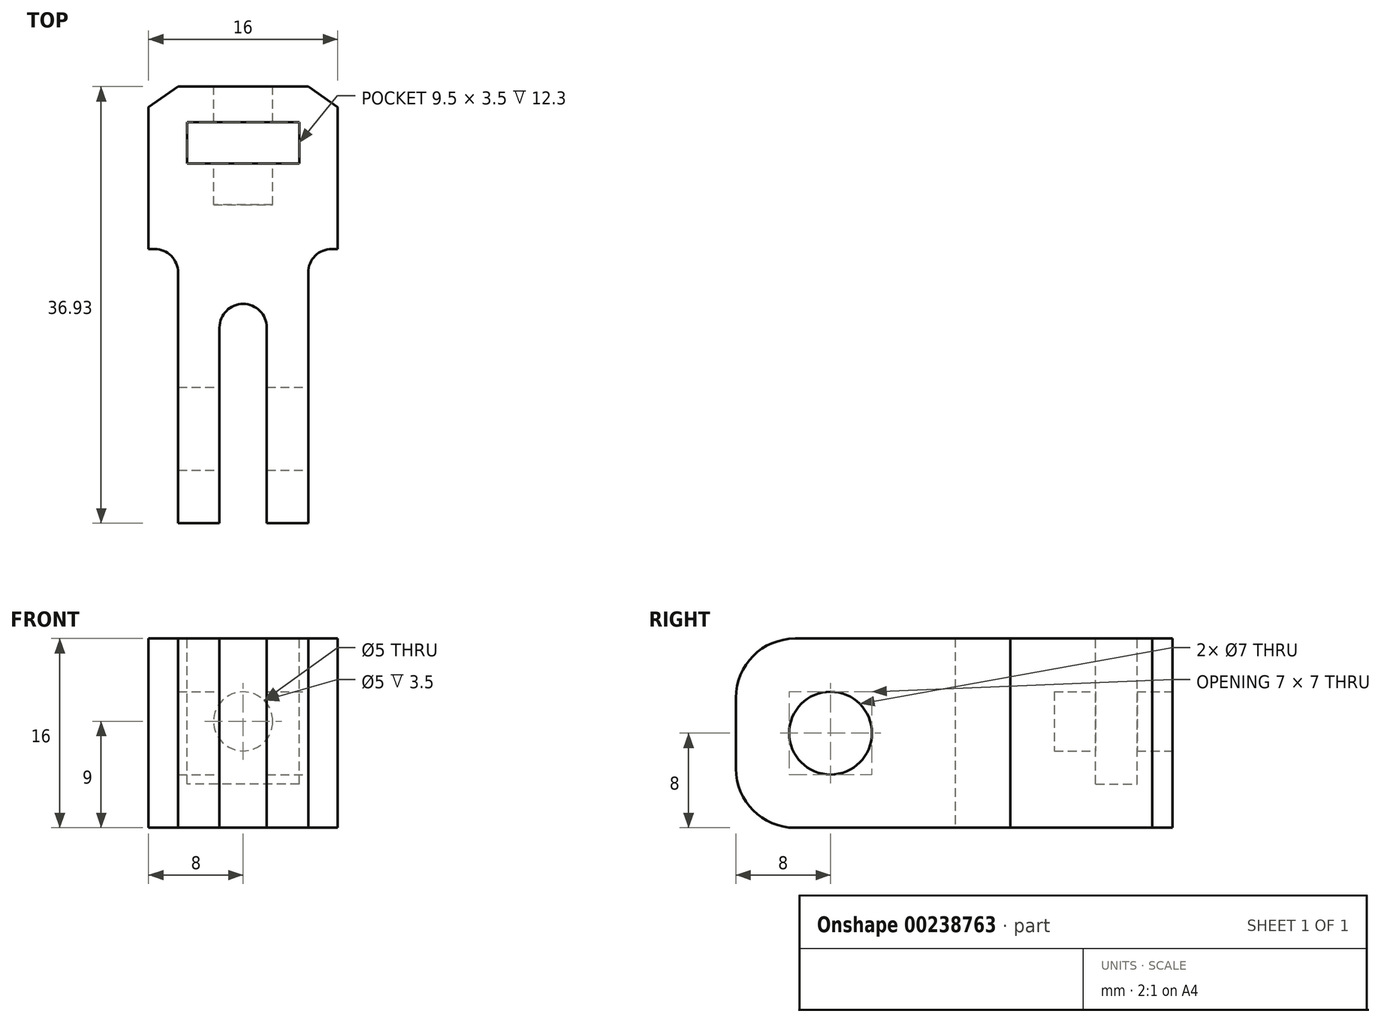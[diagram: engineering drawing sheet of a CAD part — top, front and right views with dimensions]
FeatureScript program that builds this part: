
annotation { "Feature Type Name" : "Feature", "Feature Type Description" : "" }
export const myFeature = defineFeature(function(context is Context, id is Id, definition is map)
    precondition{}
    {
        {
            var Q0;
            Q0=qCreatedBy(makeId("Top.planeOp"),FACE);
            var sketch = newSketch(context, id + "F0", { "sketchPlane" : qUnion([Q0])});
            skLineSegment(sketch, "E0.top", {"start": v(-5.5, -26) * mm, "end": v(-2, -26) * mm});
            skLineSegment(sketch, "E0.left", {"start": v(-5.5, -2.8) * mm, "end": v(-5.5, -26) * mm});
            skLineSegment(sketch, "E0.right", {"start": v(5.5, -2.8) * mm, "end": v(5.5, -26) * mm});
            skLineSegment(sketch, "E1.top", {"start": v(-2, -7.45) * mm, "end": v(2, -7.45) * mm});
            skLineSegment(sketch, "E1.left", {"start": v(-2, -26) * mm, "end": v(-2, -7.45) * mm});
            skLineSegment(sketch, "E1.right", {"start": v(2, -26) * mm, "end": v(2, -7.45) * mm});
            skLineSegment(sketch, "E2.trimOffspring", {"start": v(2, -26) * mm, "end": v(5.5, -26) * mm});
            skLineSegment(sketch, "E3.top", {"start": v(-5.5, 10.93) * mm, "end": v(5.5, 10.93) * mm});
            skLineSegment(sketch, "E4", {"start": v(0, 24.77) * mm, "end": v(0, -50.26) * mm, "construction": true});
            skPoint(sketch, "E4.startSnap0", {"position": v(0, 10.93) * mm});
            skPoint(sketch, "E4.endSnap0", {"position": v(0, -7.45) * mm});
            skLineSegment(sketch, "E5.top", {"start": v(-8, -2.8) * mm, "end": v(-5.5, -2.8) * mm});
            skLineSegment(sketch, "E5.left", {"start": v(-8, 9.2) * mm, "end": v(-8, -2.8) * mm});
            skLineSegment(sketch, "E5.right", {"start": v(8, 9.2) * mm, "end": v(8, -2.8) * mm});
            skPoint(sketch, "E5.middle", {"position": v(0, 3.2) * mm});
            skPoint(sketch, "E6.orphan", {"position": v(-5.5, 0) * mm});
            skLineSegment(sketch, "E7.trimOffspring", {"start": v(5.5, -2.8) * mm, "end": v(8, -2.8) * mm});
            skLineSegment(sketch, "E8", {"start": v(8, 9.2) * mm, "end": v(5.5, 10.93) * mm});
            skLineSegment(sketch, "E9", {"start": v(-5.5, 10.93) * mm, "end": v(-8, 9.2) * mm});
            skSolve(sketch);
        }
        {
            var Q0;
            Q0=qSketchRegion(id+"F0",true);
            extrude(context, id + "F1", {"entities" : qUnion([Q0]), "depth" : 16 * mm});
        }
        {
            var Q0;
            Q0=makeQuery(id+"F1.opExtrude","SWEPT_FACE",FACE,{"disambiguationData":[OSD([sQuery(id+"F0.wireOp",EDGE,"E3.top")])]});
            var sketch = newSketch(context, id + "F2", { "sketchPlane" : qUnion([Q0])});
            skCircle(sketch, "E10", {"center": v(0, 9) * mm, "radius": 2.5 * mm});
            skSolve(sketch);
        }
        {
            var Q0;
            Q0=qSketchRegion(id+"F2",true);
            extrude(context, id + "F3", {"entities" : qUnion([Q0]), "operationType" : NewBodyOperationType.REMOVE, "oppositeDirection" : true, "depth" : 10 * mm});
        }
        {
            var Q0;
            Q0=makeQuery(id+"F1.opExtrude","SWEPT_FACE",FACE,{"disambiguationData":[OSD([sQuery(id+"F0.wireOp",EDGE,"E0.right"),sQuery(id+"F0.wireOp",EDGE,"E3.right")])]});
            var sketch = newSketch(context, id + "F4", { "sketchPlane" : qUnion([Q0])});
            skCircle(sketch, "E11", {"center": v(-18, 8) * mm, "radius": 3.5 * mm});
            skSolve(sketch);
        }
        {
            var Q0;
            Q0=qSketchRegion(id+"F4",true);
            var Q1;
            Q1=makeQuery(id+"F1.opExtrude","SWEPT_FACE",FACE,{"disambiguationData":[OSD([sQuery(id+"F0.wireOp",EDGE,"E0.left"),sQuery(id+"F0.wireOp",EDGE,"E3.left")])]});
            extrude(context, id + "F5", {"entities" : qUnion([Q0]), "operationType" : NewBodyOperationType.REMOVE, "endBound" : BoundingType.UP_TO_SURFACE, "oppositeDirection" : true, "endBoundEntityFace" : qUnion([Q1]), "depth" : 25 * mm});
        }
        {
            var Q0;
            Q0=makeQuery(id+"F1.opExtrude","SWEPT_EDGE",EDGE,{"disambiguationData":[OSD([sQuery(id+"F0.wireOp",EDGE,"E0.left"),sQuery(id+"F0.wireOp",EDGE,"E5.top")])]});
            var Q1;
            Q1=makeQuery(id+"F1.opExtrude","SWEPT_EDGE",EDGE,{"disambiguationData":[OSD([sQuery(id+"F0.wireOp",EDGE,"E1.top"),sQuery(id+"F0.wireOp",EDGE,"E1.right")])]});
            var Q2;
            Q2=makeQuery(id+"F1.opExtrude","SWEPT_EDGE",EDGE,{"disambiguationData":[OSD([sQuery(id+"F0.wireOp",EDGE,"E1.top"),sQuery(id+"F0.wireOp",EDGE,"E1.left")])]});
            var Q3;
            Q3=makeQuery(id+"F1.opExtrude","SWEPT_EDGE",EDGE,{"disambiguationData":[OSD([sQuery(id+"F0.wireOp",EDGE,"E0.right"),sQuery(id+"F0.wireOp",EDGE,"E7.trimOffspring")])]});
            fillet(context, id + "F6", {"entities" : qUnion([Q0, Q1, Q2, Q3]), "radius" : 2 * mm, "tangentPropagation" : true, "allowEdgeOverflow" : false});
        }
        {
            var Q0;
            Q0=makeQuery(id+"F1.opExtrude","CAP_FACE",FACE,{"disambiguationData":[OSD([sQuery(id+"F0.wireOp",EDGE,"E0.top"),sQuery(id+"F0.wireOp",EDGE,"E0.left"),sQuery(id+"F0.wireOp",EDGE,"E0.right"),sQuery(id+"F0.wireOp",EDGE,"E1.top"),sQuery(id+"F0.wireOp",EDGE,"E1.left"),sQuery(id+"F0.wireOp",EDGE,"E1.right"),sQuery(id+"F0.wireOp",EDGE,"E2.trimOffspring"),sQuery(id+"F0.wireOp",EDGE,"E3.top"),sQuery(id+"F0.wireOp",EDGE,"E3.left"),sQuery(id+"F0.wireOp",EDGE,"E3.right")])],"isStart":false});
            var sketch = newSketch(context, id + "F7", { "sketchPlane" : qUnion([Q0])});
            skLineSegment(sketch, "E12.bottom", {"start": v(4.75, 4.43) * mm, "end": v(-4.75, 4.43) * mm});
            skLineSegment(sketch, "E12.top", {"start": v(4.75, 7.93) * mm, "end": v(-4.75, 7.93) * mm});
            skLineSegment(sketch, "E12.left", {"start": v(4.75, 4.43) * mm, "end": v(4.75, 7.93) * mm});
            skLineSegment(sketch, "E12.right", {"start": v(-4.75, 4.43) * mm, "end": v(-4.75, 7.93) * mm});
            skPoint(sketch, "E12.middle", {"position": v(0, 6.18) * mm});
            skSolve(sketch);
        }
        {
            var Q0;
            Q0 = qSketchRegion(id + "F7", true);
            extrude(context, id + "F8", {"entities" : qUnion([Q0]), "operationType" : NewBodyOperationType.REMOVE, "oppositeDirection" : true, "depth" : 12.3 * mm});
        }
        {
            var Q0;
            Q0=makeQuery(id+"F1.opExtrude","CAP_EDGE",EDGE,{"disambiguationData":[OSD([sQuery(id+"F0.wireOp",EDGE,"E2.trimOffspring")])],"isStart":false});
            var Q1;
            Q1=makeQuery(id+"F1.opExtrude","CAP_EDGE",EDGE,{"disambiguationData":[OSD([sQuery(id+"F0.wireOp",EDGE,"E2.trimOffspring")])],"isStart":true});
            var Q2;
            Q2=makeQuery(id+"F1.opExtrude","CAP_EDGE",EDGE,{"disambiguationData":[OSD([sQuery(id+"F0.wireOp",EDGE,"E0.top")])],"isStart":false});
            var Q3;
            Q3=makeQuery(id+"F1.opExtrude","CAP_EDGE",EDGE,{"disambiguationData":[OSD([sQuery(id+"F0.wireOp",EDGE,"E0.top")])],"isStart":true});
            fillet(context, id + "F9", {"entities" : qUnion([Q0, Q1, Q2, Q3]), "radius" : 5 * mm, "tangentPropagation" : true, "allowEdgeOverflow" : false});
        }
    });
